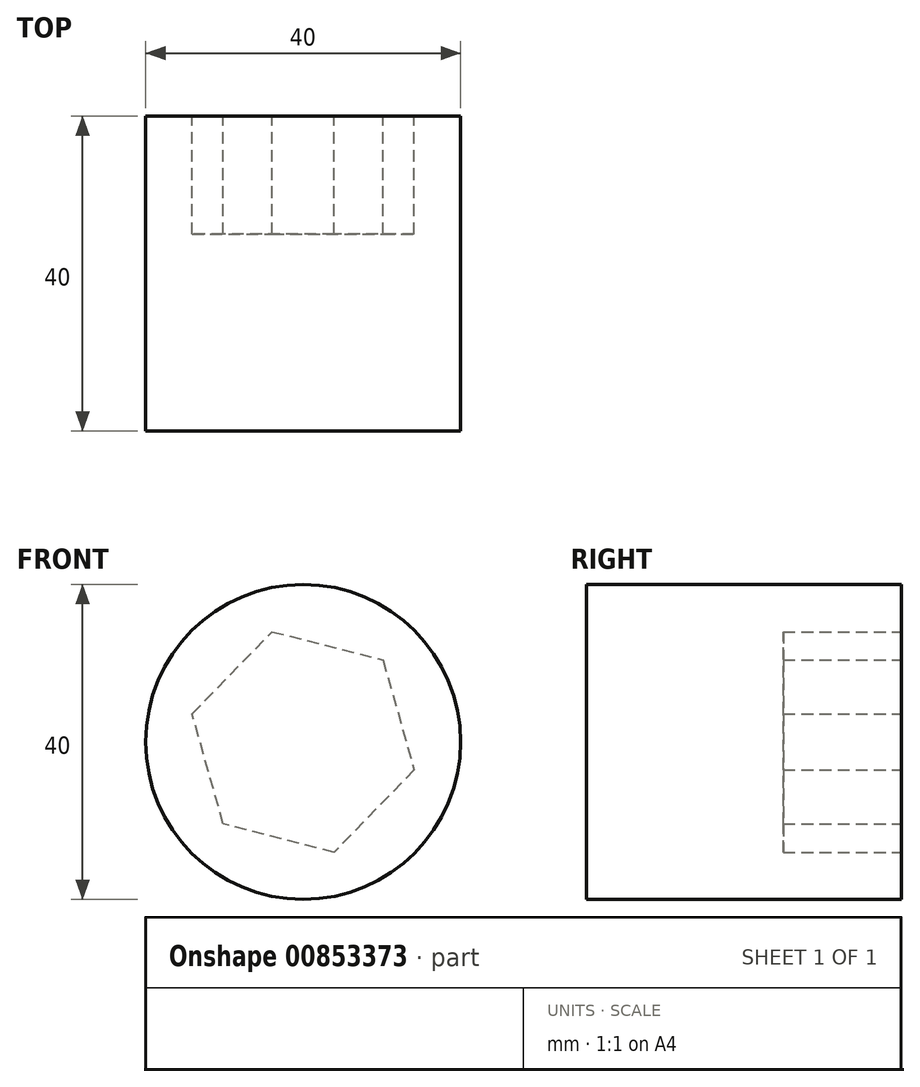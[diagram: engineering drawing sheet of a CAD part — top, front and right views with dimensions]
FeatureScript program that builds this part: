
annotation { "Feature Type Name" : "Feature", "Feature Type Description" : "" }
export const myFeature = defineFeature(function(context is Context, id is Id, definition is map)
    precondition{}
    {
        {
            var Q0;
            Q0=qCreatedBy(makeId("Front.planeOp"),FACE);
            var sketch = newSketch(context, id + "F0", { "sketchPlane" : qUnion([Q0])});
            skCircle(sketch, "E0", {"center": v(0, 0) * mm, "radius": 20 * mm});
            skSolve(sketch);
        }
        {
            var Q0;
            Q0=makeQuery(id+"F0.imprint","IMPRINT",FACE,{"disambiguationData":[TD([[makeQuery(id+"F0.imprint","IMPRINT",EDGE,{"derivedFrom":sQuery(id+"F0.wireOp",EDGE,"E0")}),1.0]])]});
            extrude(context, id + "F1", {"entities" : qUnion([Q0]), "depth" : 40 * mm, "offsetDistance" : 25 * mm});
        }
        {
            var Q0;
            Q0=qCreatedBy(makeId("Front.planeOp"),FACE);
            var sketch = newSketch(context, id + "F2", { "sketchPlane" : qUnion([Q0])});
            skCircle(sketch, "E1.cCircle", {"center": v(0, 0) * mm, "radius": 12.6 * mm, "construction": true});
            skLineSegment(sketch, "E1.0", {"start": v(14.1, -3.58) * mm, "end": v(3.95, -14) * mm});
            skLineSegment(sketch, "E1.1", {"start": v(3.95, -14) * mm, "end": v(-10.15, -10.42) * mm});
            skLineSegment(sketch, "E1.2", {"start": v(-10.15, -10.42) * mm, "end": v(-14.1, 3.58) * mm});
            skLineSegment(sketch, "E1.3", {"start": v(-14.1, 3.58) * mm, "end": v(-3.95, 14) * mm});
            skLineSegment(sketch, "E1.4", {"start": v(-3.95, 14) * mm, "end": v(10.15, 10.42) * mm});
            skLineSegment(sketch, "E1.5", {"start": v(10.15, 10.42) * mm, "end": v(14.1, -3.58) * mm});
            skPoint(sketch, "E1.0.midPoint", {"position": v(9.03, -8.79) * mm});
            skSolve(sketch);
        }
        {
            var Q0;
            Q0=makeQuery(id+"F2.imprint","IMPRINT",FACE,{"disambiguationData":[TD([[makeQuery(id+"F2.imprint","IMPRINT",EDGE,{"derivedFrom":sQuery(id+"F2.wireOp",EDGE,"E1.0")}),-1.0]])]});
            extrude(context, id + "F3", {"entities" : qUnion([Q0]), "operationType" : NewBodyOperationType.REMOVE, "depth" : 15 * mm, "offsetDistance" : 25 * mm});
        }
    });
